# Revit family: IS_Connect_Multiproduct_BIM_DE;E7723;E7724
name_source: partatom
category: Plumbing Fixtures
revit_build: Autodesk Revit MEP 2014 (Build: 20130308_1515(x64)
units: mm (PartAtom-declared; Revit-internal decimal feet)

## types (2) — shared parameters
Accessories = www.idealstandard.de\ersatzteile
AreaUnits = millimeters
Assembly Code = C1030200
AssetType = Fixed
Brand = Ideal Standard
ConnectionType = Mechanical
DurationUnit = year
ExpectedLife = 25
Finish = white
GrossWeight = 0
IfcExportAs = IfcSanitaryTerminalType
IfcExportType = SEAT&COVER
InstallationInstructions = www.idealstandard.de\produkte
LinearUnits = millimeters
ManufacturerURL = www.idealstandard.com
NBSDescription = WC Seats and covers
NBSReference = 45-30-70/384
NettWeight = 2,5 kg
NominalHeight = 50 mm
NominalLength = 430 mm
NominalWidth = 365 mm
PanColor = White
PanMaterial = Duroplast
ProductInformation = www.idealstandard.de/produkte
Shape = Sculptured
Size = 383x460x49mm
Space = Internal
URL = www.idealstandard.com
Uniclass2015Code = Pr_40_20_93_95
Uniclass2015Title = WC Seats and covers
Uniclass2015Version = Products v1.1
Version = 1
VolumeUnits = Litres
WarrantyDescription = Manufacturers Warranty
WarrantyDurationUnit = year
zero-valued in all types: CWFU, Cost, Default Elevation, HWFU, SpilloverLevel, WFU

## per-type parameters (varying)
| type | BIMObjectName | BarCode | Description | Features | Model | ModelNumber | ModelReference | Name |
| E772401 - Connect slim seat & cover | ISI_IdealStandard_WcSeatsAndCovers_Connect_E772401 | 5017830474807 | E772401 Connect slim seat & cover | Connect slim seat & cover | E772401 | E772401 | Connect slim seat & cover | WcSeatsAndCovers_Connect_E772401_IdealStandard |
| E772301 - Connect slim seat & cover, slow close | ISI_IdealStandard_WcSeatsAndCovers_Connect_E772301 | 5017830474791 | E772301 Connect slim seat & cover, slow close | Connect slim seat & cover, slow close | E772301 | E772301 | Connect slim seat & cover, slow close | WcSeatsAndCovers_Connect_E772301_IdealStandard |

## geometry (parser evidence)
native form markers: Sweep x2
no freeform markers — native parametric forms only
